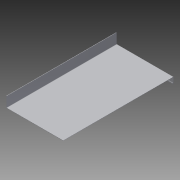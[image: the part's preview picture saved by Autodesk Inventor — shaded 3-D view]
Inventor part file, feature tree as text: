
AUTODESK INVENTOR PART (.ipt)
format: ipt  version: 2013 (Build 170138000, 138)  size: 148,480 bytes
history: native  units: in
note: dims shown in document units (in); Inventor stores cm internally (conversion verified against a paired STEP export)
features: sheet_metal_op x8, sketch x4, other x4
ambient origin geometry x8: Origin, YZ Plane, XZ Plane, XY Plane, X Axis, Y Axis, Z Axis, Center Point
bodies: Solid1 (feature_tree)
feature tree (16):
  sheet_metal_op  "Face1"
  sheet_metal_op  "Flange1"
  sheet_metal_op  "Hem1"
  sheet_metal_op  "Flange2"
  sketch  "Sketch1"  dims[d0=21.5in]
  other  "Plate1"
  sketch  "Sketch2"  dims[d1=42.0in]
  other  "Plate2"
  sheet_metal_op  "Bend1"
  sheet_metal_op  "Corner1"
  sketch  "Sketch4"  dims[d3=0.12in d4=0.06in d5=0.24in d6=0.12in d7=2.5in d8=90.0deg d9=0.12in d10=0.48in d11=0.12in d12=0.12in d13=0.12in d14=0.06in d15=0.24in d16=0.12in d17=0.48in d18=0.06in d19=0.03in d20=0.12in d21=0.06in d22=0.24in d23=0.12in d24=4.0in d25=90.0deg d26=0.12in d27=0.48in d28=0.12in d29=0.12in]
  other  "Plate3"
  sheet_metal_op  "Bend2"
  sheet_metal_op  "Corner2"
  sketch  "Sketch3"  dims[d2=0.12in]
  other  "Definition1"
